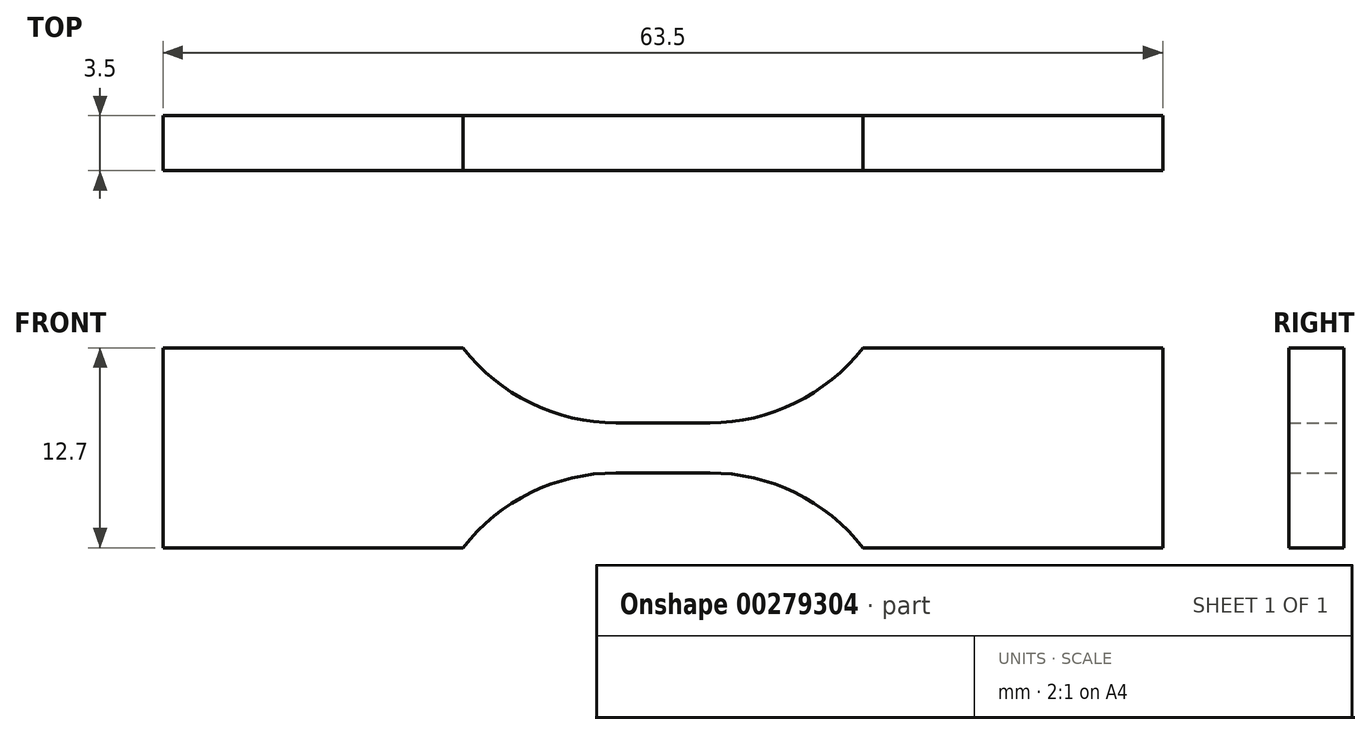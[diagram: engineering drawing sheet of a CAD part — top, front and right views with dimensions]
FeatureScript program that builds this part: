
annotation { "Feature Type Name" : "Feature", "Feature Type Description" : "" }
export const myFeature = defineFeature(function(context is Context, id is Id, definition is map)
    precondition{}
    {
        {
            var Q0;
            Q0=qCreatedBy(makeId("Front.planeOp"),FACE);
            var sketch = newSketch(context, id + "F0", { "sketchPlane" : qUnion([Q0])});
            skLineSegment(sketch, "E0", {"start": v(0, 1.59) * mm, "end": v(2.98, 1.59) * mm});
            skArc(sketch, "E1", {"start": v(2.98, 1.6) * mm, "mid": v(8.4, 2.84) * mm, "end": v(12.7, 6.35) * mm});
            skLineSegment(sketch, "E2", {"start": v(12.7, 6.35) * mm, "end": v(31.75, 6.35) * mm});
            skLineSegment(sketch, "E3", {"start": v(31.75, 6.35) * mm, "end": v(31.75, 0) * mm});
            skLineSegment(sketch, "E4.MirrorCS", {"start": v(0, -1.59) * mm, "end": v(2.98, -1.59) * mm});
            skLineSegment(sketch, "E5.MirrorCS", {"start": v(31.75, -6.35) * mm, "end": v(31.75, 0) * mm});
            skLineSegment(sketch, "E6.MirrorCS", {"start": v(12.7, -6.35) * mm, "end": v(31.75, -6.35) * mm});
            skArc(sketch, "E7.MirrorCS", {"start": v(2.98, -1.6) * mm, "mid": v(8.4, -2.84) * mm, "end": v(12.7, -6.35) * mm});
            skLineSegment(sketch, "E8.MirrorCS", {"start": v(-31.75, -6.35) * mm, "end": v(-31.75, 0) * mm});
            skLineSegment(sketch, "E9.MirrorCS", {"start": v(-12.7, 6.35) * mm, "end": v(-31.75, 6.35) * mm});
            skLineSegment(sketch, "E10.MirrorCS", {"start": v(0, 1.6) * mm, "end": v(-2.98, 1.59) * mm});
            skLineSegment(sketch, "E11.MirrorCS", {"start": v(-31.75, 6.35) * mm, "end": v(-31.75, 0) * mm});
            skArc(sketch, "E12.MirrorCS", {"start": v(-2.98, -1.6) * mm, "mid": v(-8.4, -2.84) * mm, "end": v(-12.7, -6.35) * mm});
            skArc(sketch, "E13.MirrorCS", {"start": v(-2.98, 1.6) * mm, "mid": v(-8.4, 2.84) * mm, "end": v(-12.7, 6.35) * mm});
            skLineSegment(sketch, "E14.MirrorCS", {"start": v(-12.7, -6.35) * mm, "end": v(-31.75, -6.35) * mm});
            skLineSegment(sketch, "E15.MirrorCS", {"start": v(0, -1.59) * mm, "end": v(-2.98, -1.59) * mm});
            skSolve(sketch);
        }
        {
            var Q0;
            Q0 = qSketchRegion(id + "F0", true);
            extrude(context, id + "F1", {"entities" : qUnion([Q0]), "endBound" : BoundingType.SYMMETRIC, "depth" : 3.5 * mm});
        }
    });
